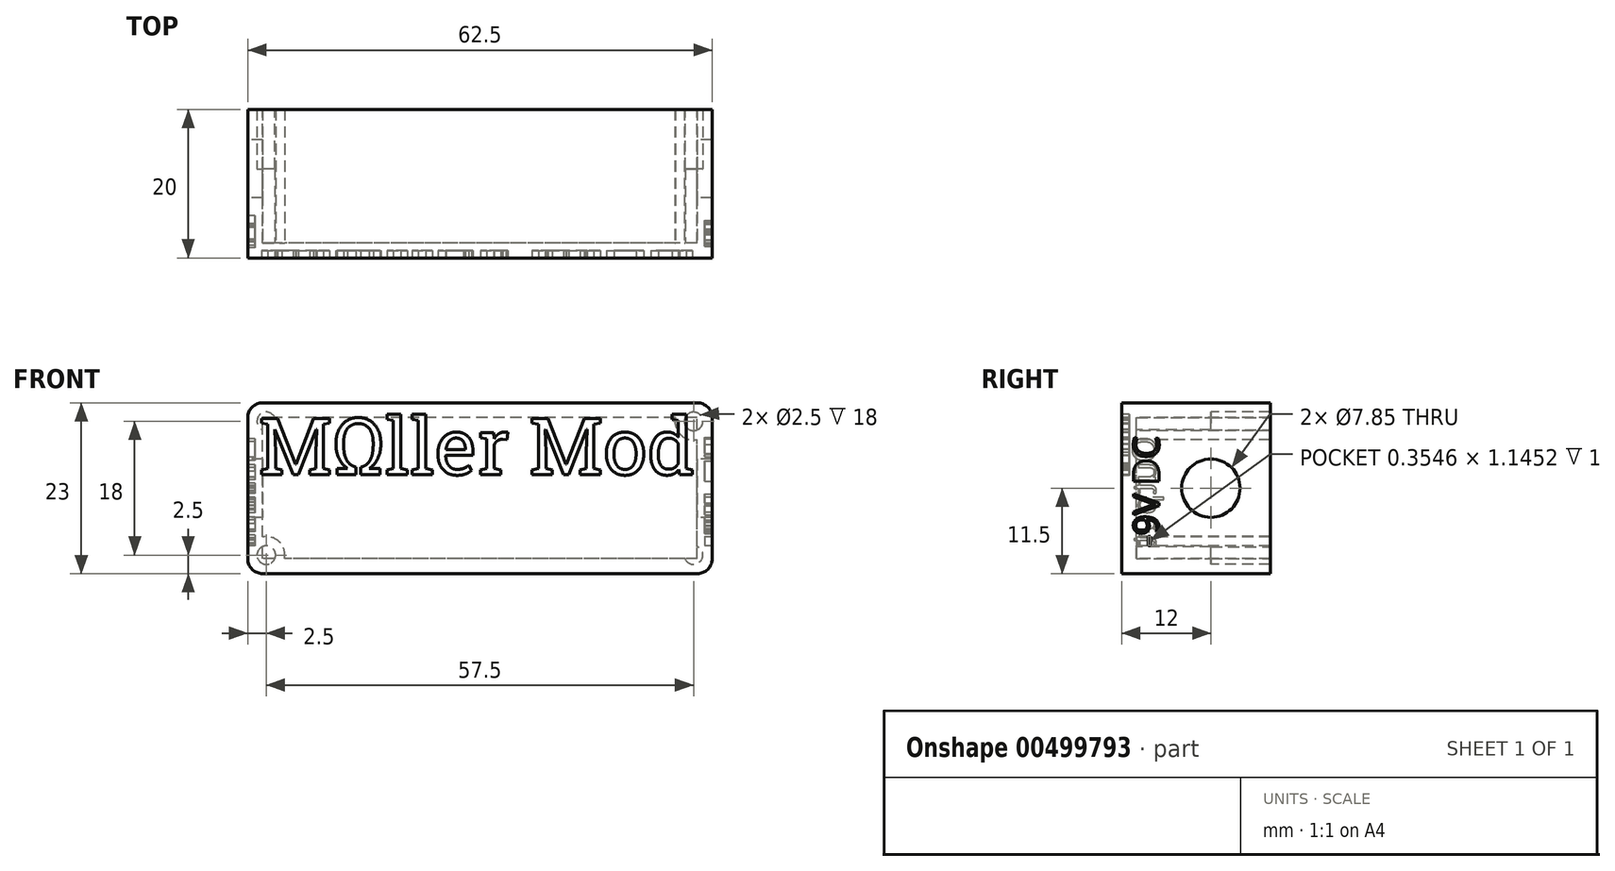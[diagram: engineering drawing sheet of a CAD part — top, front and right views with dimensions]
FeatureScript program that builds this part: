
annotation { "Feature Type Name" : "Feature", "Feature Type Description" : "" }
export const myFeature = defineFeature(function(context is Context, id is Id, definition is map)
    precondition{}
    {
        {
            var Q0;
            Q0=qCreatedBy(makeId("Front.planeOp"),FACE);
            var sketch = newSketch(context, id + "F0", { "sketchPlane" : qUnion([Q0])});
            skLineSegment(sketch, "E0.bottom", {"start": v(31.25, -11.5) * mm, "end": v(-31.25, -11.5) * mm});
            skLineSegment(sketch, "E0.top", {"start": v(31.25, 11.5) * mm, "end": v(-31.25, 11.5) * mm});
            skLineSegment(sketch, "E0.left", {"start": v(31.25, -11.5) * mm, "end": v(31.25, 11.5) * mm});
            skLineSegment(sketch, "E0.right", {"start": v(-31.25, -11.5) * mm, "end": v(-31.25, 11.5) * mm});
            skPoint(sketch, "E0.middle", {"position": v(0, 0) * mm});
            skSolve(sketch);
        }
        {
            var Q0;
            Q0=makeQuery(id+"F0.imprint","IMPRINT",FACE,{"disambiguationData":[TD([[makeQuery(id+"F0.imprint","IMPRINT",EDGE,{"derivedFrom":sQuery(id+"F0.wireOp",EDGE,"E0.bottom")}),-1.0]])]});
            extrude(context, id + "F1", {"entities" : qUnion([Q0]), "depth" : 20 * mm});
        }
        {
            var Q0;
            Q0=makeQuery(id+"F1.opExtrude","CAP_FACE",FACE,{"disambiguationData":[OSD([sQuery(id+"F0.wireOp",EDGE,"E0.bottom"),sQuery(id+"F0.wireOp",EDGE,"E0.top"),sQuery(id+"F0.wireOp",EDGE,"E0.left"),sQuery(id+"F0.wireOp",EDGE,"E0.right")])],"isStart":true});
            shell(context, id + "F2", {"entities" : qUnion([Q0]), "thickness" : 2 * mm});
        }
        {
            var Q0;
            Q0=makeQuery(id+"F1.opExtrude","SWEPT_FACE",FACE,{"disambiguationData":[OSD([sQuery(id+"F0.wireOp",EDGE,"E0.right")])]});
            var sketch = newSketch(context, id + "F3", { "sketchPlane" : qUnion([Q0])});
            skCircle(sketch, "E1", {"center": v(8, 0) * mm, "radius": 3.92 * mm});
            skSolve(sketch);
        }
        {
            var Q0;
            Q0=makeQuery(id+"F3.imprint","IMPRINT",FACE,{"disambiguationData":[TD([[makeQuery(id+"F3.imprint","IMPRINT",EDGE,{"derivedFrom":sQuery(id+"F3.wireOp",EDGE,"E1")}),1.0]])]});
            var Q1;
            Q1=sQuery(id+"F3.wireOp",EDGE,"E1");
            extrude(context, id + "F4", {"entities" : qUnion([Q0]), "operationType" : NewBodyOperationType.REMOVE, "surfaceEntities" : qUnion([Q1]), "endBound" : BoundingType.THROUGH_ALL, "oppositeDirection" : true, "depth" : 25 * mm});
        }
        {
            var Q0;
            Q0=makeQuery(id+"F1.opExtrude","SWEPT_EDGE",EDGE,{"disambiguationData":[OSD([sQuery(id+"F0.wireOp",EDGE,"E0.top"),sQuery(id+"F0.wireOp",EDGE,"E0.right")])]});
            var Q1;
            Q1=makeQuery(id+"F1.opExtrude","SWEPT_EDGE",EDGE,{"disambiguationData":[OSD([sQuery(id+"F0.wireOp",EDGE,"E0.bottom"),sQuery(id+"F0.wireOp",EDGE,"E0.right")])]});
            var Q2;
            Q2=makeQuery(id+"F1.opExtrude","SWEPT_EDGE",EDGE,{"disambiguationData":[OSD([sQuery(id+"F0.wireOp",EDGE,"E0.top"),sQuery(id+"F0.wireOp",EDGE,"E0.left")])]});
            var Q3;
            Q3=makeQuery(id+"F1.opExtrude","SWEPT_EDGE",EDGE,{"disambiguationData":[OSD([sQuery(id+"F0.wireOp",EDGE,"E0.bottom"),sQuery(id+"F0.wireOp",EDGE,"E0.left")])]});
            fillet(context, id + "F5", {"entities" : qUnion([Q0, Q1, Q2, Q3]), "radius" : 2 * mm, "tangentPropagation" : true, "allowEdgeOverflow" : false});
        }
        {
            var Q0;
            Q0=makeQuery(id+"F1.opExtrude","CAP_FACE",FACE,{"disambiguationData":[OSD([sQuery(id+"F0.wireOp",EDGE,"E0.bottom"),sQuery(id+"F0.wireOp",EDGE,"E0.top"),sQuery(id+"F0.wireOp",EDGE,"E0.left"),sQuery(id+"F0.wireOp",EDGE,"E0.right")])],"isStart":false});
            var sketch = newSketch(context, id + "F6", { "sketchPlane" : qUnion([Q0])});
            skText(sketch, "E2", { "text": "MΩller Mod", "fontName": "RobotoSlab-Regular.ttf"});
            const initialGuessF6  = {"E2": [-0.02975, 0.00184, 1, 0, 0.00766]};
            skSetInitialGuess(sketch, initialGuessF6);
            skSolve(sketch);
        }
        {
            var Q0;
            Q0 = qSketchRegion(id + "F6", true);
            extrude(context, id + "F7", {"entities" : qUnion([Q0]), "operationType" : NewBodyOperationType.REMOVE, "oppositeDirection" : true, "depth" : 1 * mm});
        }
        {
            var Q0;
            Q0=makeQuery(id+"F1.opExtrude","SWEPT_FACE",FACE,{"disambiguationData":[OSD([sQuery(id+"F0.wireOp",EDGE,"E0.left")])]});
            var sketch = newSketch(context, id + "F8", { "sketchPlane" : qUnion([Q0])});
            skText(sketch, "E3", { "text": "-9V DC\n", "fontName": "OpenSans-Regular.ttf"});
            const initialGuessF8  = {"E3": [-0.01499, -0.00786, 0, 1, 0.00344]};
            skSetInitialGuess(sketch, initialGuessF8);
            skSolve(sketch);
        }
        {
            var Q0;
            Q0=makeQuery(id+"F8.imprint","IMPRINT",FACE,{"disambiguationData":[TD([[makeQuery(id+"F8.imprint","IMPRINT",EDGE,{"derivedFrom":sQuery(id+"F8.wireOp",EDGE,"E3.sketch_text.stroke-46")}),1.0]])]});
            var Q1;
            Q1 = qSketchRegion(id + "F8", true);
            extrude(context, id + "F9", {"entities" : qUnion([Q0, Q1]), "operationType" : NewBodyOperationType.REMOVE, "oppositeDirection" : true, "depth" : 1 * mm});
        }
        {
            var Q0;
            Q0=makeQuery(id+"F1.opExtrude","SWEPT_FACE",FACE,{"disambiguationData":[OSD([sQuery(id+"F0.wireOp",EDGE,"E0.right")])]});
            var sketch = newSketch(context, id + "F10", { "sketchPlane" : qUnion([Q0])});
            skText(sketch, "E4", { "text": "Output\n", "fontName": "OpenSans-Regular.ttf"});
            const initialGuessF10  = {"E4": [0.0154, 0.00695, 0, -1, 0.0032]};
            skSetInitialGuess(sketch, initialGuessF10);
            skSolve(sketch);
        }
        {
            var Q0;
            Q0 = qSketchRegion(id + "F10", true);
            extrude(context, id + "F11", {"entities" : qUnion([Q0]), "operationType" : NewBodyOperationType.REMOVE, "oppositeDirection" : true, "depth" : 1 * mm});
        }
        {
            var Q0;
            Q0=makeQuery(id+"F2.opShell","OFFSET_FACE",FACE,{"disambiguationData":[OSD([sQuery(id+"F0.wireOp",EDGE,"E0.bottom"),sQuery(id+"F0.wireOp",EDGE,"E0.top"),sQuery(id+"F0.wireOp",EDGE,"E0.left"),sQuery(id+"F0.wireOp",EDGE,"E0.right")])]});
            var sketch = newSketch(context, id + "F12", { "sketchPlane" : qUnion([Q0])});
            skPoint(sketch, "E5", {"position": v(-28.75, 9) * mm});
            skCircle(sketch, "E6", {"center": v(-28.75, 9) * mm, "radius": 2.5 * mm});
            skCircle(sketch, "E7", {"center": v(-28.75, 9) * mm, "radius": 1.25 * mm});
            skCircle(sketch, "E8.MirrorC", {"center": v(28.75, 9) * mm, "radius": 2.5 * mm});
            skCircle(sketch, "E9.MirrorC", {"center": v(28.75, 9) * mm, "radius": 1.25 * mm});
            skCircle(sketch, "E10.MirrorC", {"center": v(-28.75, -9) * mm, "radius": 2.5 * mm});
            skCircle(sketch, "E11.MirrorC", {"center": v(-28.75, -9) * mm, "radius": 1.25 * mm});
            skCircle(sketch, "E12.MirrorC", {"center": v(28.75, -9) * mm, "radius": 2.5 * mm});
            skCircle(sketch, "E13.MirrorC", {"center": v(28.75, -9) * mm, "radius": 1.25 * mm});
            skSolve(sketch);
        }
        {
            var Q0;
            {var subQ0=sQuery(id+"F12.wireOp",EDGE,"E6");var subQ1=sQuery(id+"F0.wireOp",EDGE,"E0.top");var subQ2=makeQuery(id+"F2.opShell","OFFSET_EDGE",EDGE,{"disambiguationData":[OSD([subQ1]),TDD([makeQuery(id+"F1.opExtrude","CAP_EDGE",EDGE,{"disambiguationData":[OSD([subQ1])],"isStart":false})])]});var subQ3=makeQuery(id+"F12.imprint","INTERSECT",VERTEX,{"derivedFrom":[subQ2,subQ0]});Q0=makeQuery(id+"F12.imprint","IMPRINT",FACE,{"disambiguationData":[TD([[makeQuery(id+"F12.imprint","IMPRINT",EDGE,{"disambiguationData":[TD([[subQ3,1.0]])],"derivedFrom":subQ0}),1.0]])]});}
            var Q1;
            {var subQ0=sQuery(id+"F12.wireOp",EDGE,"E10.MirrorC");var subQ1=sQuery(id+"F0.wireOp",EDGE,"E0.bottom");var subQ2=makeQuery(id+"F2.opShell","OFFSET_EDGE",EDGE,{"disambiguationData":[OSD([subQ1]),TDD([makeQuery(id+"F1.opExtrude","CAP_EDGE",EDGE,{"disambiguationData":[OSD([subQ1])],"isStart":false})])]});var subQ3=makeQuery(id+"F12.imprint","INTERSECT",VERTEX,{"derivedFrom":[subQ2,subQ0]});Q1=makeQuery(id+"F12.imprint","IMPRINT",FACE,{"disambiguationData":[TD([[makeQuery(id+"F12.imprint","IMPRINT",EDGE,{"disambiguationData":[TD([[subQ3,1.0]])],"derivedFrom":subQ0}),-1.0]])]});}
            var Q2;
            {var subQ0=sQuery(id+"F12.wireOp",EDGE,"E8.MirrorC");var subQ1=sQuery(id+"F0.wireOp",EDGE,"E0.top");var subQ2=makeQuery(id+"F2.opShell","OFFSET_EDGE",EDGE,{"disambiguationData":[OSD([subQ1]),TDD([makeQuery(id+"F1.opExtrude","CAP_EDGE",EDGE,{"disambiguationData":[OSD([subQ1])],"isStart":false})])]});var subQ3=makeQuery(id+"F12.imprint","INTERSECT",VERTEX,{"derivedFrom":[subQ2,subQ0]});Q2=makeQuery(id+"F12.imprint","IMPRINT",FACE,{"disambiguationData":[TD([[makeQuery(id+"F12.imprint","IMPRINT",EDGE,{"disambiguationData":[TD([[subQ3,1.0]])],"derivedFrom":subQ0}),-1.0]])]});}
            var Q3;
            {var subQ0=sQuery(id+"F12.wireOp",EDGE,"E12.MirrorC");var subQ1=sQuery(id+"F0.wireOp",EDGE,"E0.bottom");var subQ2=makeQuery(id+"F2.opShell","OFFSET_EDGE",EDGE,{"disambiguationData":[OSD([subQ1]),TDD([makeQuery(id+"F1.opExtrude","CAP_EDGE",EDGE,{"disambiguationData":[OSD([subQ1])],"isStart":false})])]});var subQ3=makeQuery(id+"F12.imprint","INTERSECT",VERTEX,{"derivedFrom":[subQ2,subQ0]});Q3=makeQuery(id+"F12.imprint","IMPRINT",FACE,{"disambiguationData":[TD([[makeQuery(id+"F12.imprint","IMPRINT",EDGE,{"disambiguationData":[TD([[subQ3,1.0]])],"derivedFrom":subQ0}),1.0]])]});}
            extrude(context, id + "F13", {"entities" : qUnion([Q0, Q1, Q2, Q3]), "operationType" : NewBodyOperationType.ADD, "depth" : 18 * mm, "offsetDistance" : 25 * mm});
        }
        {
            var Q0;
            {var subQ0=sQuery(id+"F0.wireOp",EDGE,"E0.right");var subQ1=sQuery(id+"F0.wireOp",EDGE,"E0.bottom");var subQ2=sQuery(id+"F0.wireOp",EDGE,"E0.left");var subQ3=sQuery(id+"F0.wireOp",EDGE,"E0.top");Q0=makeQuery(id+"F13.boolean.opBoolean","MERGE",FACE,{"derivedFrom":[makeQuery(id+"F1.opExtrude","CAP_FACE",FACE,{"disambiguationData":[OSD([subQ1,subQ3,subQ2,subQ0])],"isStart":true}),makeQuery(id+"F13.opExtrude","CAP_FACE",FACE,{"disambiguationData":[OSD([subQ3,subQ2,sQuery(id+"F12.wireOp",EDGE,"E6"),sQuery(id+"F12.wireOp",EDGE,"E7")])],"isStart":false}),makeQuery(id+"F13.opExtrude","CAP_FACE",FACE,{"disambiguationData":[OSD([subQ3,subQ0,sQuery(id+"F12.wireOp",EDGE,"E8.MirrorC"),sQuery(id+"F12.wireOp",EDGE,"E9.MirrorC")])],"isStart":false}),makeQuery(id+"F13.opExtrude","CAP_FACE",FACE,{"disambiguationData":[OSD([subQ1,subQ2,sQuery(id+"F12.wireOp",EDGE,"E10.MirrorC"),sQuery(id+"F12.wireOp",EDGE,"E11.MirrorC")])],"isStart":false}),makeQuery(id+"F13.opExtrude","CAP_FACE",FACE,{"disambiguationData":[OSD([subQ1,subQ0,sQuery(id+"F12.wireOp",EDGE,"E12.MirrorC"),sQuery(id+"F12.wireOp",EDGE,"E13.MirrorC")])],"isStart":false})]});}
            var sketch = newSketch(context, id + "F14", { "sketchPlane" : qUnion([Q0])});
            skPoint(sketch, "E14", {"position": v(-28.75, 9) * mm});
            skCircle(sketch, "E15", {"center": v(-28.75, 9) * mm, "radius": 1.25 * mm});
            skCircle(sketch, "E16.MirrorC", {"center": v(28.75, 9) * mm, "radius": 1.25 * mm});
            skCircle(sketch, "E17.MirrorC", {"center": v(-28.75, -9) * mm, "radius": 1.25 * mm});
            skCircle(sketch, "E18.MirrorC", {"center": v(28.75, -9) * mm, "radius": 1.25 * mm});
            skSolve(sketch);
        }
        {
            var Q0;
            {var subQ1=sQuery(id+"F0.wireOp",EDGE,"E0.left");var subQ2=makeQuery(id+"F2.opShell","OFFSET_FACE",FACE,{"disambiguationData":[OSD([subQ1])]});var subQ4=sQuery(id+"F0.wireOp",EDGE,"E0.top");var subQ14=makeQuery(id+"F13.boolean.opBoolean","SPLIT",EDGE,{"disambiguationData":[TD([subQ2])],"derivedFrom":makeQuery(id+"F2.opShell","OFFSET_EDGE",EDGE,{"disambiguationData":[OSD([subQ4]),TDD([makeQuery(id+"F1.opExtrude","CAP_EDGE",EDGE,{"disambiguationData":[OSD([subQ4])],"isStart":true})])]})});Q0=makeQuery(id+"F14.imprint","IMPRINT",FACE,{"disambiguationData":[TD([[makeQuery(id+"F14.imprint","IMPRINT",EDGE,{"derivedFrom":subQ14}),1.0]])]});}
            var Q1;
            {var subQ1=sQuery(id+"F0.wireOp",EDGE,"E0.left");var subQ4=makeQuery(id+"F2.opShell","OFFSET_FACE",FACE,{"disambiguationData":[OSD([subQ1])]});var subQ7=sQuery(id+"F0.wireOp",EDGE,"E0.bottom");var subQ14=makeQuery(id+"F13.boolean.opBoolean","SPLIT",EDGE,{"disambiguationData":[TD([subQ4])],"derivedFrom":makeQuery(id+"F2.opShell","OFFSET_EDGE",EDGE,{"disambiguationData":[OSD([subQ7]),TDD([makeQuery(id+"F1.opExtrude","CAP_EDGE",EDGE,{"disambiguationData":[OSD([subQ7])],"isStart":true})])]})});Q1=makeQuery(id+"F14.imprint","IMPRINT",FACE,{"disambiguationData":[TD([[makeQuery(id+"F14.imprint","IMPRINT",EDGE,{"derivedFrom":subQ14}),-1.0]])]});}
            var Q2;
            {var subQ4=sQuery(id+"F0.wireOp",EDGE,"E0.right");var subQ5=makeQuery(id+"F2.opShell","OFFSET_FACE",FACE,{"disambiguationData":[OSD([subQ4])]});var subQ6=sQuery(id+"F0.wireOp",EDGE,"E0.bottom");var subQ14=makeQuery(id+"F13.boolean.opBoolean","SPLIT",EDGE,{"disambiguationData":[TD([subQ5])],"derivedFrom":makeQuery(id+"F2.opShell","OFFSET_EDGE",EDGE,{"disambiguationData":[OSD([subQ6]),TDD([makeQuery(id+"F1.opExtrude","CAP_EDGE",EDGE,{"disambiguationData":[OSD([subQ6])],"isStart":true})])]})});Q2=makeQuery(id+"F14.imprint","IMPRINT",FACE,{"disambiguationData":[TD([[makeQuery(id+"F14.imprint","IMPRINT",EDGE,{"derivedFrom":subQ14}),-1.0]])]});}
            var Q3;
            {var subQ1=sQuery(id+"F0.wireOp",EDGE,"E0.right");var subQ2=makeQuery(id+"F2.opShell","OFFSET_FACE",FACE,{"disambiguationData":[OSD([subQ1])]});var subQ4=sQuery(id+"F0.wireOp",EDGE,"E0.top");var subQ14=makeQuery(id+"F13.boolean.opBoolean","SPLIT",EDGE,{"disambiguationData":[TD([subQ2])],"derivedFrom":makeQuery(id+"F2.opShell","OFFSET_EDGE",EDGE,{"disambiguationData":[OSD([subQ4]),TDD([makeQuery(id+"F1.opExtrude","CAP_EDGE",EDGE,{"disambiguationData":[OSD([subQ4])],"isStart":true})])]})});Q3=makeQuery(id+"F14.imprint","IMPRINT",FACE,{"disambiguationData":[TD([[makeQuery(id+"F14.imprint","IMPRINT",EDGE,{"derivedFrom":subQ14}),1.0]])]});}
            var Q4;
            Q4=sQuery(id+"F14.wireOp",EDGE,"E15");
            var Q5;
            Q5=sQuery(id+"F14.wireOp",EDGE,"E17.MirrorC");
            var Q6;
            Q6=sQuery(id+"F14.wireOp",EDGE,"E16.MirrorC");
            var Q7;
            Q7=sQuery(id+"F14.wireOp",EDGE,"E18.MirrorC");
            extrude(context, id + "F15", {"entities" : qUnion([Q0, Q1, Q2, Q3]), "operationType" : NewBodyOperationType.REMOVE, "surfaceEntities" : qUnion([Q4, Q5, Q6, Q7]), "oppositeDirection" : true, "depth" : 8 * mm, "offsetDistance" : 25 * mm});
        }
    });
